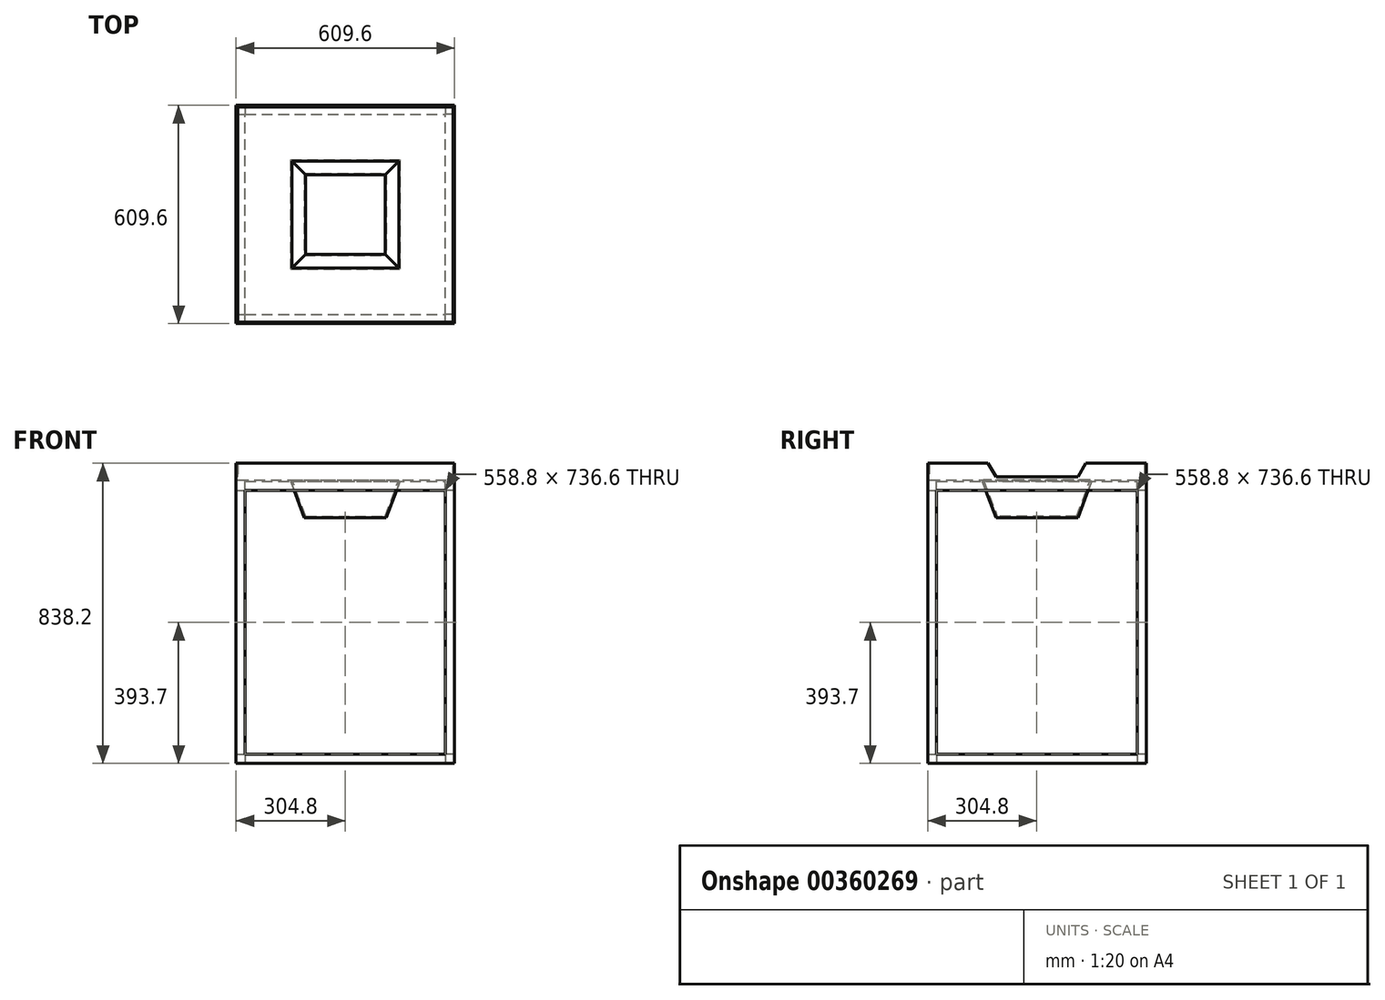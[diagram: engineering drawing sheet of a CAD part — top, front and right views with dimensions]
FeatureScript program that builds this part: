
annotation { "Feature Type Name" : "Feature", "Feature Type Description" : "" }
export const myFeature = defineFeature(function(context is Context, id is Id, definition is map)
    precondition{}
    {
        {
            var Q0;
            Q0=qCreatedBy(makeId("Top.planeOp"),FACE);
            var sketch = newSketch(context, id + "F0", { "sketchPlane" : qUnion([Q0])});
            skLineSegment(sketch, "E0.bottom", {"start": v(0, 0) * mm, "end": v(609.6, 0) * mm});
            skLineSegment(sketch, "E0.top", {"start": v(0, 609.6) * mm, "end": v(609.6, 609.6) * mm});
            skLineSegment(sketch, "E0.left", {"start": v(0, 0) * mm, "end": v(0, 609.6) * mm});
            skLineSegment(sketch, "E0.right", {"start": v(609.6, 0) * mm, "end": v(609.6, 609.6) * mm});
            skSolve(sketch);
        }
        {
            var Q0;
            Q0=makeQuery(id+"F0.imprint","IMPRINT",FACE,{"disambiguationData":[TD([[makeQuery(id+"F0.imprint","IMPRINT",EDGE,{"derivedFrom":sQuery(id+"F0.wireOp",EDGE,"E0.bottom")}),1.0]])]});
            extrude(context, id + "F1", {"entities" : qUnion([Q0]), "depth" : 50.8 * mm});
        }
        {
            var Q0;
            {var subQ0=sQuery(id+"F0.wireOp",EDGE,"E0.left");var subQ1=sQuery(id+"F0.wireOp",EDGE,"E0.top");var subQ2=sQuery(id+"F0.wireOp",EDGE,"E0.right");var subQ3=sQuery(id+"F0.wireOp",EDGE,"E0.bottom");var subQ4=makeQuery(id+"F1.opExtrude","CAP_FACE",FACE,{"disambiguationData":[OSD([subQ3,subQ1,subQ0,subQ2])],"isStart":true});Q0=makeQuery(id+"F8.boolean.opBoolean","SPLIT",FACE,{"disambiguationData":[TD([makeQuery(id+"F1.opExtrude","SWEPT_FACE",FACE,{"disambiguationData":[OSD([subQ3])]}),subQ4,makeQuery(id+"F1.opExtrude","SWEPT_FACE",FACE,{"disambiguationData":[OSD([subQ1])]}),makeQuery(id+"F1.opExtrude","SWEPT_FACE",FACE,{"disambiguationData":[OSD([subQ0])]}),makeQuery(id+"F1.opExtrude","SWEPT_FACE",FACE,{"disambiguationData":[OSD([subQ2])]}),makeQuery(id+"F8.opExtrude","SWEPT_FACE",FACE,{"disambiguationData":[OSD([sQuery(id+"F7.wireOp",EDGE,"71ce93d1-072a-4c4b-a0da-8e84aa0d43b3")])]}),makeQuery(id+"F8.opExtrude","SWEPT_FACE",FACE,{"disambiguationData":[OSD([sQuery(id+"F7.wireOp",EDGE,"617cd770-b13a-485e-a092-c3328c9f167f")])]}),makeQuery(id+"F8.opExtrude","SWEPT_FACE",FACE,{"disambiguationData":[OSD([sQuery(id+"F7.wireOp",EDGE,"ddc54c5b-ed15-43ca-a465-0adad0c44a69")])]}),makeQuery(id+"F8.opExtrude","SWEPT_FACE",FACE,{"disambiguationData":[OSD([sQuery(id+"F7.wireOp",EDGE,"84db9d79-833e-4565-b0e3-43fa11b1d89b")])]})])],"derivedFrom":subQ4});}
            var sketch = newSketch(context, id + "F2", { "sketchPlane" : qUnion([Q0])});
            skLineSegment(sketch, "E1.bottom", {"start": v(152.4, -457.2) * mm, "end": v(457.2, -457.2) * mm});
            skLineSegment(sketch, "E1.top", {"start": v(152.4, -152.4) * mm, "end": v(457.2, -152.4) * mm});
            skLineSegment(sketch, "E1.left", {"start": v(152.4, -457.2) * mm, "end": v(152.4, -152.4) * mm});
            skLineSegment(sketch, "E1.right", {"start": v(457.2, -457.2) * mm, "end": v(457.2, -152.4) * mm});
            skSolve(sketch);
        }
        {
            var Q0;
            Q0=makeQuery(id+"F2.imprint","IMPRINT",FACE,{"disambiguationData":[TD([[makeQuery(id+"F2.imprint","IMPRINT",EDGE,{"derivedFrom":sQuery(id+"F2.wireOp",EDGE,"E1.bottom")}),-1.0]])]});
            cPlane(context, id + "F3", {"entities" : qUnion([Q0]), "cplaneType" : CPlaneType.OFFSET, "offset" : 101.6 * mm, "width" : 152.4 * mm, "height" : 152.4 * mm});
        }
        {
            var Q0;
            Q0=qCreatedBy(id+"F3.planeOp",FACE);
            var sketch = newSketch(context, id + "F4", { "sketchPlane" : qUnion([Q0])});
            skLineSegment(sketch, "E2.bottom", {"start": v(190.5, -419.1) * mm, "end": v(419.1, -419.1) * mm});
            skLineSegment(sketch, "E2.top", {"start": v(190.5, -190.5) * mm, "end": v(419.1, -190.5) * mm});
            skLineSegment(sketch, "E2.left", {"start": v(190.5, -419.1) * mm, "end": v(190.5, -190.5) * mm});
            skLineSegment(sketch, "E2.right", {"start": v(419.1, -419.1) * mm, "end": v(419.1, -190.5) * mm});
            skSolve(sketch);
        }
        {
            var Q1;
            Q1 = qSketchRegion(id + "F2", true);
            var Q2;
            Q2 = qSketchRegion(id + "F4", true);
            loft(context, id + "F5", {"operationType" : NewBodyOperationType.ADD, "sheetProfilesArray" : [{ "sheetProfileEntities" : qUnion([Q1]) }, { "sheetProfileEntities" : qUnion([Q2]) }]});
        }
        {
            var Q0;
            Q0=makeQuery(id+"F1.opExtrude","CAP_FACE",FACE,{"disambiguationData":[OSD([sQuery(id+"F0.wireOp",EDGE,"E0.bottom"),sQuery(id+"F0.wireOp",EDGE,"E0.top"),sQuery(id+"F0.wireOp",EDGE,"E0.left"),sQuery(id+"F0.wireOp",EDGE,"E0.right")])],"isStart":false});
            shell(context, id + "F6", {"entities" : qUnion([Q0]), "thickness" : 4.76 * mm});
        }
        {
            var Q0;
            Q0=makeQuery(id+"F1.opExtrude","CAP_FACE",FACE,{"disambiguationData":[OSD([sQuery(id+"F0.wireOp",EDGE,"E0.bottom"),sQuery(id+"F0.wireOp",EDGE,"E0.top"),sQuery(id+"F0.wireOp",EDGE,"E0.left"),sQuery(id+"F0.wireOp",EDGE,"E0.right")])],"isStart":true});
            var sketch = newSketch(context, id + "F7", { "sketchPlane" : qUnion([Q0])});
            skLineSegment(sketch, "E3.bottom", {"start": v(0, 0) * mm, "end": v(609.6, 0) * mm});
            skLineSegment(sketch, "E3.top", {"start": v(0, -609.6) * mm, "end": v(609.6, -609.6) * mm});
            skLineSegment(sketch, "E3.left", {"start": v(0, 0) * mm, "end": v(0, -609.6) * mm});
            skLineSegment(sketch, "E3.right", {"start": v(609.6, 0) * mm, "end": v(609.6, -609.6) * mm});
            skLineSegment(sketch, "E4.0", {"start": v(25.4, -25.4) * mm, "end": v(584.2, -25.4) * mm});
            skLineSegment(sketch, "E4.1", {"start": v(25.4, -25.4) * mm, "end": v(25.4, -584.2) * mm});
            skLineSegment(sketch, "E4.2", {"start": v(25.4, -584.2) * mm, "end": v(584.2, -584.2) * mm});
            skLineSegment(sketch, "E4.3", {"start": v(584.2, -25.4) * mm, "end": v(584.2, -584.2) * mm});
            skSolve(sketch);
        }
        {
            var Q0;
            Q0 = qSketchRegion(id + "F7", true);
            extrude(context, id + "F8", {"entities" : qUnion([Q0]), "operationType" : NewBodyOperationType.ADD, "depth" : 25.4 * mm});
        }
        {
            var Q0;
            Q0=makeQuery(id+"F1.opExtrude","SWEPT_FACE",FACE,{"disambiguationData":[OSD([sQuery(id+"F0.wireOp",EDGE,"E0.left")])]});
            var sketch = newSketch(context, id + "F9", { "sketchPlane" : qUnion([Q0])});
            skLineSegment(sketch, "E5", {"start": v(-419.1, 12.7) * mm, "end": v(-441.1, 50.8) * mm});
            skLineSegment(sketch, "E6", {"start": v(-441.1, 50.8) * mm, "end": v(-168.5, 50.8) * mm});
            skLineSegment(sketch, "E7", {"start": v(-168.5, 50.8) * mm, "end": v(-190.5, 12.7) * mm});
            skLineSegment(sketch, "E8", {"start": v(-190.5, 12.7) * mm, "end": v(-419.1, 12.7) * mm});
            skSolve(sketch);
        }
        {
            var Q0;
            Q0=makeQuery(id+"F9.imprint","IMPRINT",FACE,{"disambiguationData":[TD([[makeQuery(id+"F9.imprint","IMPRINT",EDGE,{"derivedFrom":sQuery(id+"F9.wireOp",EDGE,"E5")}),-1.0]])]});
            extrude(context, id + "F10", {"entities" : qUnion([Q0]), "operationType" : NewBodyOperationType.REMOVE, "endBound" : BoundingType.THROUGH_ALL, "oppositeDirection" : true, "depth" : 25.4 * mm});
        }
        {
            var Q0;
            Q0=makeQuery(id+"F8.opExtrude","CAP_FACE",FACE,{"disambiguationData":[OSD([sQuery(id+"F7.wireOp",EDGE,"E3.bottom"),sQuery(id+"F7.wireOp",EDGE,"E3.top"),sQuery(id+"F7.wireOp",EDGE,"E3.left"),sQuery(id+"F7.wireOp",EDGE,"E3.right"),sQuery(id+"F7.wireOp",EDGE,"E4.0"),sQuery(id+"F7.wireOp",EDGE,"E4.1"),sQuery(id+"F7.wireOp",EDGE,"E4.2"),sQuery(id+"F7.wireOp",EDGE,"E4.3")])],"isStart":false});
            var sketch = newSketch(context, id + "F11", { "sketchPlane" : qUnion([Q0])});
            skLineSegment(sketch, "E9.bottom", {"start": v(0, 0) * mm, "end": v(25.4, 0) * mm});
            skLineSegment(sketch, "E9.top", {"start": v(0, -25.4) * mm, "end": v(25.4, -25.4) * mm});
            skLineSegment(sketch, "E9.left", {"start": v(0, 0) * mm, "end": v(0, -25.4) * mm});
            skLineSegment(sketch, "E9.right", {"start": v(25.4, 0) * mm, "end": v(25.4, -25.4) * mm});
            skLineSegment(sketch, "E10.bottom", {"start": v(609.6, 0) * mm, "end": v(584.2, 0) * mm});
            skLineSegment(sketch, "E10.top", {"start": v(609.6, -25.4) * mm, "end": v(584.2, -25.4) * mm});
            skLineSegment(sketch, "E10.left", {"start": v(609.6, 0) * mm, "end": v(609.6, -25.4) * mm});
            skLineSegment(sketch, "E10.right", {"start": v(584.2, 0) * mm, "end": v(584.2, -25.4) * mm});
            skLineSegment(sketch, "E11.bottom", {"start": v(609.6, -609.6) * mm, "end": v(584.2, -609.6) * mm});
            skLineSegment(sketch, "E11.top", {"start": v(609.6, -584.2) * mm, "end": v(584.2, -584.2) * mm});
            skLineSegment(sketch, "E11.left", {"start": v(609.6, -609.6) * mm, "end": v(609.6, -584.2) * mm});
            skLineSegment(sketch, "E11.right", {"start": v(584.2, -609.6) * mm, "end": v(584.2, -584.2) * mm});
            skLineSegment(sketch, "E12.bottom", {"start": v(0, -609.6) * mm, "end": v(25.4, -609.6) * mm});
            skLineSegment(sketch, "E12.top", {"start": v(0, -584.2) * mm, "end": v(25.4, -584.2) * mm});
            skLineSegment(sketch, "E12.left", {"start": v(0, -609.6) * mm, "end": v(0, -584.2) * mm});
            skLineSegment(sketch, "E12.right", {"start": v(25.4, -609.6) * mm, "end": v(25.4, -584.2) * mm});
            skSolve(sketch);
        }
        {
            var Q0;
            Q0 = qSketchRegion(id + "F11", true);
            extrude(context, id + "F12", {"entities" : qUnion([Q0]), "operationType" : NewBodyOperationType.ADD, "depth" : 762 * mm});
        }
        {
            var Q0;
            Q0=makeQuery(id+"F12.opExtrude","CAP_FACE",FACE,{"disambiguationData":[OSD([sQuery(id+"F11.wireOp",EDGE,"E9.bottom"),sQuery(id+"F11.wireOp",EDGE,"E9.top"),sQuery(id+"F11.wireOp",EDGE,"E9.left"),sQuery(id+"F11.wireOp",EDGE,"E9.right")])],"isStart":false});
            var sketch = newSketch(context, id + "F13", { "sketchPlane" : qUnion([Q0])});
            skLineSegment(sketch, "E13.bottom", {"start": v(0, 0) * mm, "end": v(609.6, 0) * mm});
            skLineSegment(sketch, "E13.top", {"start": v(0, -609.6) * mm, "end": v(609.6, -609.6) * mm});
            skLineSegment(sketch, "E13.left", {"start": v(0, 0) * mm, "end": v(0, -609.6) * mm});
            skLineSegment(sketch, "E13.right", {"start": v(609.6, 0) * mm, "end": v(609.6, -609.6) * mm});
            skLineSegment(sketch, "E14.0", {"start": v(25.4, -25.4) * mm, "end": v(25.4, -584.2) * mm});
            skLineSegment(sketch, "E14.1", {"start": v(25.4, -25.4) * mm, "end": v(584.2, -25.4) * mm});
            skLineSegment(sketch, "E14.2", {"start": v(584.2, -25.4) * mm, "end": v(584.2, -584.2) * mm});
            skLineSegment(sketch, "E14.3", {"start": v(25.4, -584.2) * mm, "end": v(584.2, -584.2) * mm});
            skSolve(sketch);
        }
        {
            var Q0;
            Q0 = qSketchRegion(id + "F13", true);
            extrude(context, id + "F14", {"entities" : qUnion([Q0]), "operationType" : NewBodyOperationType.ADD, "oppositeDirection" : true, "depth" : 25.4 * mm});
        }
    });
